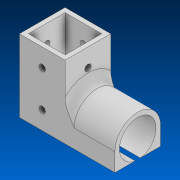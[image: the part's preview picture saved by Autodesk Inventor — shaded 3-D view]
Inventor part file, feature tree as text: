
AUTODESK INVENTOR PART (.ipt)
format: ipt  version: 2022 (Build 260153000, 153)  size: 161,280 bytes
history: native  units: in
note: dims shown in document units (in); Inventor stores cm internally (conversion verified against a paired STEP export)
features: sketch x4, extrude x3, hole x2, fillet x1
ambient origin geometry x8: Origin, YZ Plane, XZ Plane, XY Plane, X Axis, Y Axis, Z Axis, Center Point
bodies: Solid1 (feature_tree)
feature tree (10):
  extrude  "Extrusion1"  Depth=1.01in
  hole  "Hole1"  [1 undecoded]
  hole  "Hole2"  [1 undecoded]
  sketch  "Sketch4"  dims[d7=0.175in d8=0.75in d9=0.375in d10=0.25in d11=0.5635in d12=1.0in d13=0.8108in d14=0.175in d15=0.75in d16=0.375in d17=0.25in d18=0.5635in d19=1.0in d20=0.8108in d21=1.375in d22=0.0in d23=2.0in d24=0.0in d25=0.25in d26=1.0in d27=1.01in d28=0.5in d29=0.0344in d30=0.5in d31=0.0344in]
  extrude  "Extrusion2"  Depth=0.25in TaperAngle=0.0deg
  extrude  "Extrusion3"  Depth=0.25in TaperAngle=0.0deg
  fillet  "Fillet1"  Radius=0.25in
  sketch  "Sketch1"  dims[d0=1.01in d1=1.01in]
  sketch  "Sketch2"  dims[d2=0.125in d3=2.0in d4=0.0in]
  sketch  "Sketch3"  dims[d5=0.5in d6=1.0in]
note: 2 required parameter values undecoded (feature->parameter linkage not recoverable at this tier; creation-order binding heuristic only, values carry confidence <= 0.55)
